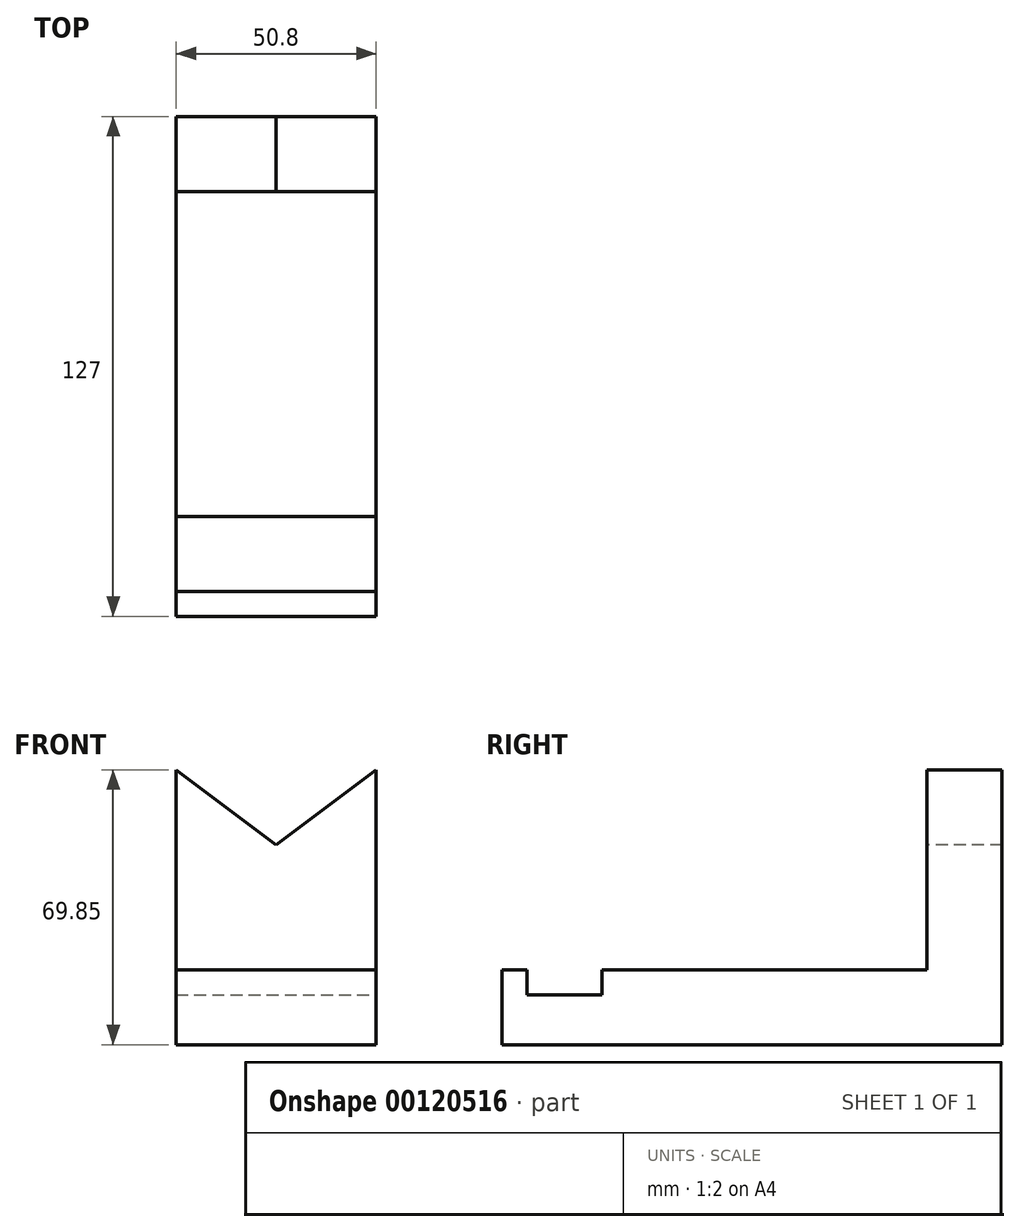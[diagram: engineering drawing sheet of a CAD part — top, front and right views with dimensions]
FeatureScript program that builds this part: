
annotation { "Feature Type Name" : "Feature", "Feature Type Description" : "" }
export const myFeature = defineFeature(function(context is Context, id is Id, definition is map)
    precondition{}
    {
        {
            var Q0;
            Q0=qCreatedBy(makeId("Top.planeOp"),FACE);
            var sketch = newSketch(context, id + "F0", { "sketchPlane" : qUnion([Q0])});
            skLineSegment(sketch, "E0.bottom", {"start": v(25.4, 63.5) * mm, "end": v(-25.4, 63.5) * mm});
            skLineSegment(sketch, "E0.top", {"start": v(25.4, -63.5) * mm, "end": v(-25.4, -63.5) * mm});
            skLineSegment(sketch, "E0.left", {"start": v(25.4, 63.5) * mm, "end": v(25.4, -63.5) * mm});
            skLineSegment(sketch, "E0.right", {"start": v(-25.4, 63.5) * mm, "end": v(-25.4, -63.5) * mm});
            skPoint(sketch, "E0.middle", {"position": v(0, 0) * mm});
            skSolve(sketch);
        }
        {
            var Q0;
            Q0 = qSketchRegion(id + "F0", true);
            extrude(context, id + "F1", {"entities" : qUnion([Q0]), "depth" : 19.05 * mm});
        }
        {
            var Q0;
            Q0=makeQuery(id+"F1.opExtrude","CAP_FACE",FACE,{"disambiguationData":[OSD([sQuery(id+"F0.wireOp",EDGE,"E0.bottom"),sQuery(id+"F0.wireOp",EDGE,"E0.top"),sQuery(id+"F0.wireOp",EDGE,"E0.left"),sQuery(id+"F0.wireOp",EDGE,"E0.right")])],"isStart":false});
            var sketch = newSketch(context, id + "F2", { "sketchPlane" : qUnion([Q0])});
            skLineSegment(sketch, "E1.bottom", {"start": v(-25.4, -38.1) * mm, "end": v(25.4, -38.1) * mm});
            skLineSegment(sketch, "E1.top", {"start": v(-25.4, -57.15) * mm, "end": v(25.4, -57.15) * mm});
            skLineSegment(sketch, "E1.left", {"start": v(-25.4, -38.1) * mm, "end": v(-25.4, -57.15) * mm});
            skLineSegment(sketch, "E1.right", {"start": v(25.4, -38.1) * mm, "end": v(25.4, -57.15) * mm});
            skSolve(sketch);
        }
        {
            var Q0;
            Q0 = qSketchRegion(id + "F2", true);
            extrude(context, id + "F3", {"entities" : qUnion([Q0]), "operationType" : NewBodyOperationType.REMOVE, "oppositeDirection" : true, "depth" : 6.35 * mm});
        }
        {
            var Q0;
            {var subQ0=sQuery(id+"F0.wireOp",EDGE,"E0.bottom");var subQ1=sQuery(id+"F0.wireOp",EDGE,"E0.left");var subQ2=sQuery(id+"F0.wireOp",EDGE,"E0.right");Q0=makeQuery(id+"F3.boolean.opBoolean","SPLIT",FACE,{"disambiguationData":[TD([makeQuery(id+"F1.opExtrude","SWEPT_FACE",FACE,{"disambiguationData":[OSD([subQ0])]})])],"derivedFrom":makeQuery(id+"F1.opExtrude","CAP_FACE",FACE,{"disambiguationData":[OSD([subQ0,sQuery(id+"F0.wireOp",EDGE,"E0.top"),subQ1,subQ2])],"isStart":false})});}
            var sketch = newSketch(context, id + "F4", { "sketchPlane" : qUnion([Q0])});
            skLineSegment(sketch, "E2.bottom", {"start": v(25.4, 44.45) * mm, "end": v(-25.4, 44.45) * mm});
            skLineSegment(sketch, "E2.top", {"start": v(25.4, 63.5) * mm, "end": v(-25.4, 63.5) * mm});
            skLineSegment(sketch, "E2.left", {"start": v(25.4, 44.45) * mm, "end": v(25.4, 63.5) * mm});
            skLineSegment(sketch, "E2.right", {"start": v(-25.4, 44.45) * mm, "end": v(-25.4, 63.5) * mm});
            skSolve(sketch);
        }
        {
            var Q0;
            Q0 = qSketchRegion(id + "F4", true);
            extrude(context, id + "F5", {"entities" : qUnion([Q0]), "operationType" : NewBodyOperationType.ADD, "depth" : 50.8 * mm});
        }
        {
            var Q0;
            Q0=makeQuery(id+"F5.opExtrude","SWEPT_FACE",FACE,{"disambiguationData":[OSD([sQuery(id+"F4.wireOp",EDGE,"E2.bottom")])]});
            var sketch = newSketch(context, id + "F6", { "sketchPlane" : qUnion([Q0])});
            skLineSegment(sketch, "E3", {"start": v(0, 69.85) * mm, "end": v(0, 50.8) * mm});
            skPoint(sketch, "E3.endSnap0", {"position": v(0, 69.85) * mm});
            skLineSegment(sketch, "E4", {"start": v(0, 50.8) * mm, "end": v(25.4, 69.85) * mm});
            skLineSegment(sketch, "E5", {"start": v(25.4, 69.85) * mm, "end": v(0, 50.8) * mm});
            skLineSegment(sketch, "E6", {"start": v(0, 50.8) * mm, "end": v(-25.4, 69.85) * mm});
            skLineSegment(sketch, "E7", {"start": v(-25.4, 69.85) * mm, "end": v(25.4, 69.85) * mm});
            skSolve(sketch);
        }
        {
            var Q0;
            Q0 = qSketchRegion(id + "F6", true);
            extrude(context, id + "F7", {"entities" : qUnion([Q0]), "operationType" : NewBodyOperationType.REMOVE, "endBound" : BoundingType.THROUGH_ALL, "oppositeDirection" : true, "depth" : 25.4 * mm, "hasSecondDirection" : true, "secondDirectionBound" : SecondDirectionBoundingType.THROUGH_ALL, "secondDirectionOppositeDirection" : false, "secondDirectionDepth" : 25.4 * mm});
        }
    });
